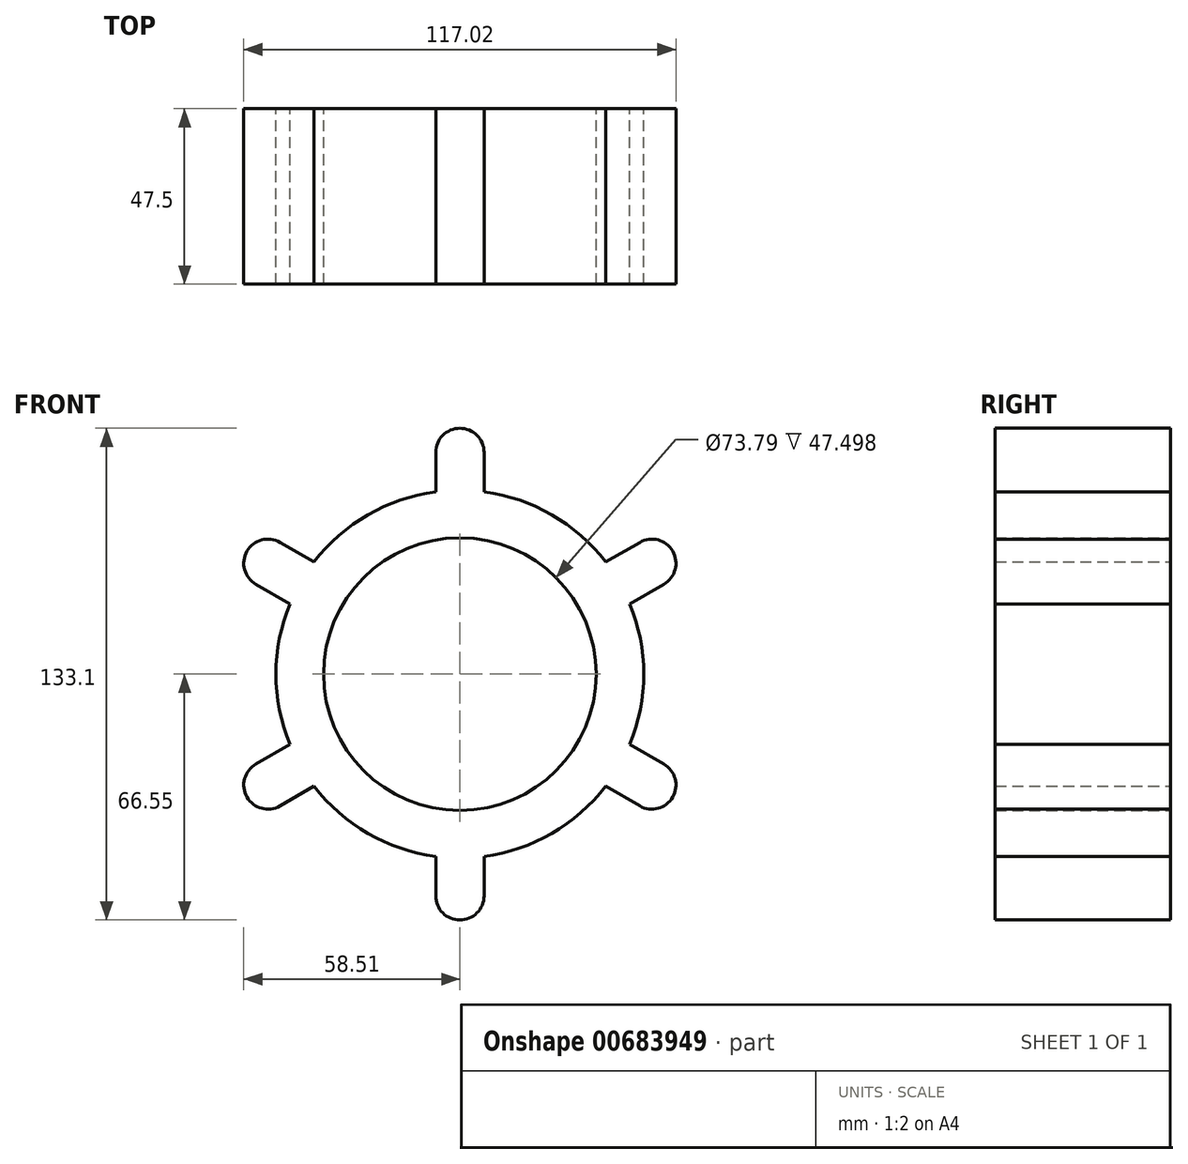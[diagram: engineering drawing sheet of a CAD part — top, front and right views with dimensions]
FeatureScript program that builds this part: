
annotation { "Feature Type Name" : "Feature", "Feature Type Description" : "" }
export const myFeature = defineFeature(function(context is Context, id is Id, definition is map)
    precondition{}
    {
        {
            var Q0;
            Q0=qCreatedBy(makeId("Front.planeOp"),FACE);
            var sketch = newSketch(context, id + "F0", { "sketchPlane" : qUnion([Q0])});
            skCircle(sketch, "E0", {"center": v(0, 0) * mm, "radius": 36.9 * mm});
            skCircle(sketch, "E1", {"center": v(0, 0) * mm, "radius": 49.79 * mm});
            skLineSegment(sketch, "E2.top", {"start": v(6.54, 39.57) * mm, "end": v(-6.54, 39.57) * mm});
            skLineSegment(sketch, "E2.left", {"start": v(6.54, 60) * mm, "end": v(6.54, 39.57) * mm});
            skLineSegment(sketch, "E2.right", {"start": v(-6.54, 60) * mm, "end": v(-6.54, 39.57) * mm});
            skPoint(sketch, "E2.middle", {"position": v(0, 49.79) * mm});
            skArc(sketch, "E3", {"start": v(6.54, 60) * mm, "mid": v(0, 66.55) * mm, "end": v(-6.54, 60) * mm});
            skLineSegment(sketch, "E4.1.0", {"start": v(-55.24, 24.34) * mm, "end": v(-37.54, 14.12) * mm});
            skArc(sketch, "E4.1.1", {"start": v(-48.7, 35.67) * mm, "mid": v(-57.63, 33.27) * mm, "end": v(-55.24, 24.34) * mm});
            skLineSegment(sketch, "E4.1.2", {"start": v(-48.7, 35.67) * mm, "end": v(-31, 25.45) * mm});
            skLineSegment(sketch, "E4.1.3", {"start": v(-31, 25.45) * mm, "end": v(-37.54, 14.12) * mm});
            skLineSegment(sketch, "E4.2.0", {"start": v(-48.7, -35.67) * mm, "end": v(-31, -25.45) * mm});
            skArc(sketch, "E4.2.1", {"start": v(-55.24, -24.34) * mm, "mid": v(-57.63, -33.27) * mm, "end": v(-48.7, -35.67) * mm});
            skLineSegment(sketch, "E4.2.2", {"start": v(-55.24, -24.34) * mm, "end": v(-37.54, -14.12) * mm});
            skLineSegment(sketch, "E4.2.3", {"start": v(-37.54, -14.12) * mm, "end": v(-31, -25.45) * mm});
            skLineSegment(sketch, "E4.3.0", {"start": v(6.54, -60) * mm, "end": v(6.54, -39.57) * mm});
            skArc(sketch, "E4.3.1", {"start": v(-6.54, -60) * mm, "mid": v(0, -66.55) * mm, "end": v(6.54, -60) * mm});
            skLineSegment(sketch, "E4.3.2", {"start": v(-6.54, -60) * mm, "end": v(-6.54, -39.57) * mm});
            skLineSegment(sketch, "E4.3.3", {"start": v(-6.54, -39.57) * mm, "end": v(6.54, -39.57) * mm});
            skLineSegment(sketch, "E4.4.0", {"start": v(55.24, -24.34) * mm, "end": v(37.54, -14.12) * mm});
            skArc(sketch, "E4.4.1", {"start": v(48.7, -35.67) * mm, "mid": v(57.63, -33.27) * mm, "end": v(55.24, -24.34) * mm});
            skLineSegment(sketch, "E4.4.2", {"start": v(48.7, -35.67) * mm, "end": v(31, -25.45) * mm});
            skLineSegment(sketch, "E4.4.3", {"start": v(31, -25.45) * mm, "end": v(37.54, -14.12) * mm});
            skLineSegment(sketch, "E4.5.0", {"start": v(48.7, 35.67) * mm, "end": v(31, 25.45) * mm});
            skArc(sketch, "E4.5.1", {"start": v(55.24, 24.34) * mm, "mid": v(57.63, 33.27) * mm, "end": v(48.7, 35.67) * mm});
            skLineSegment(sketch, "E4.5.2", {"start": v(55.24, 24.34) * mm, "end": v(37.54, 14.12) * mm});
            skLineSegment(sketch, "E4.5.3", {"start": v(37.54, 14.12) * mm, "end": v(31, 25.45) * mm});
            skSolve(sketch);
        }
        {
            var Q0;
            Q0=makeQuery(id+"F0.imprint","IMPRINT",FACE,{"disambiguationData":[TD([[makeQuery(id+"F0.imprint","IMPRINT",EDGE,{"derivedFrom":sQuery(id+"F0.wireOp",EDGE,"E0")}),-1.0]])]});
            var Q1;
            {var subQ5=sQuery(id+"F0.wireOp",EDGE,"E4.1.3");Q1=makeQuery(id+"F0.imprint","IMPRINT",FACE,{"disambiguationData":[TD([[makeQuery(id+"F0.imprint","IMPRINT",EDGE,{"derivedFrom":subQ5}),-1.0]])]});}
            var Q2;
            {var subQ5=sQuery(id+"F0.wireOp",EDGE,"E4.1.1");Q2=makeQuery(id+"F0.imprint","IMPRINT",FACE,{"disambiguationData":[TD([[makeQuery(id+"F0.imprint","IMPRINT",EDGE,{"derivedFrom":subQ5}),1.0]])]});}
            var Q3;
            {var subQ5=sQuery(id+"F0.wireOp",EDGE,"E4.2.3");Q3=makeQuery(id+"F0.imprint","IMPRINT",FACE,{"disambiguationData":[TD([[makeQuery(id+"F0.imprint","IMPRINT",EDGE,{"derivedFrom":subQ5}),-1.0]])]});}
            var Q4;
            {var subQ5=sQuery(id+"F0.wireOp",EDGE,"E4.2.1");Q4=makeQuery(id+"F0.imprint","IMPRINT",FACE,{"disambiguationData":[TD([[makeQuery(id+"F0.imprint","IMPRINT",EDGE,{"derivedFrom":subQ5}),1.0]])]});}
            var Q5;
            {var subQ5=sQuery(id+"F0.wireOp",EDGE,"E4.3.1");Q5=makeQuery(id+"F0.imprint","IMPRINT",FACE,{"disambiguationData":[TD([[makeQuery(id+"F0.imprint","IMPRINT",EDGE,{"derivedFrom":subQ5}),1.0]])]});}
            var Q6;
            {var subQ5=sQuery(id+"F0.wireOp",EDGE,"E4.3.3");Q6=makeQuery(id+"F0.imprint","IMPRINT",FACE,{"disambiguationData":[TD([[makeQuery(id+"F0.imprint","IMPRINT",EDGE,{"derivedFrom":subQ5}),-1.0]])]});}
            var Q7;
            {var subQ5=sQuery(id+"F0.wireOp",EDGE,"E4.4.3");Q7=makeQuery(id+"F0.imprint","IMPRINT",FACE,{"disambiguationData":[TD([[makeQuery(id+"F0.imprint","IMPRINT",EDGE,{"derivedFrom":subQ5}),-1.0]])]});}
            var Q8;
            {var subQ5=sQuery(id+"F0.wireOp",EDGE,"E4.4.1");Q8=makeQuery(id+"F0.imprint","IMPRINT",FACE,{"disambiguationData":[TD([[makeQuery(id+"F0.imprint","IMPRINT",EDGE,{"derivedFrom":subQ5}),1.0]])]});}
            var Q9;
            {var subQ5=sQuery(id+"F0.wireOp",EDGE,"E4.5.3");Q9=makeQuery(id+"F0.imprint","IMPRINT",FACE,{"disambiguationData":[TD([[makeQuery(id+"F0.imprint","IMPRINT",EDGE,{"derivedFrom":subQ5}),-1.0]])]});}
            var Q10;
            {var subQ5=sQuery(id+"F0.wireOp",EDGE,"E4.5.1");Q10=makeQuery(id+"F0.imprint","IMPRINT",FACE,{"disambiguationData":[TD([[makeQuery(id+"F0.imprint","IMPRINT",EDGE,{"derivedFrom":subQ5}),1.0]])]});}
            var Q11;
            {var subQ5=sQuery(id+"F0.wireOp",EDGE,"E2.top");Q11=makeQuery(id+"F0.imprint","IMPRINT",FACE,{"disambiguationData":[TD([[makeQuery(id+"F0.imprint","IMPRINT",EDGE,{"derivedFrom":subQ5}),-1.0]])]});}
            var Q12;
            {var subQ5=sQuery(id+"F0.wireOp",EDGE,"E3");Q12=makeQuery(id+"F0.imprint","IMPRINT",FACE,{"disambiguationData":[TD([[makeQuery(id+"F0.imprint","IMPRINT",EDGE,{"derivedFrom":subQ5}),1.0]])]});}
            extrude(context, id + "F1", {"entities" : qUnion([Q0, Q1, Q2, Q3, Q4, Q5, Q6, Q7, Q8, Q9, Q10, Q11, Q12]), "depth" : 5.08 * mm, "offsetDistance" : 25.4 * mm});
        }
        {
            var Q0;
            Q0=makeQuery(id+"F1.opExtrude","CAP_FACE",FACE,{"disambiguationData":[OSD([sQuery(id+"F0.wireOp",EDGE,"E0"),sQuery(id+"F0.wireOp",EDGE,"E1"),sQuery(id+"F0.wireOp",EDGE,"E2.left"),sQuery(id+"F0.wireOp",EDGE,"E2.right"),sQuery(id+"F0.wireOp",EDGE,"E3"),sQuery(id+"F0.wireOp",EDGE,"E4.1.0"),sQuery(id+"F0.wireOp",EDGE,"E4.1.1"),sQuery(id+"F0.wireOp",EDGE,"E4.1.2"),sQuery(id+"F0.wireOp",EDGE,"E4.2.0"),sQuery(id+"F0.wireOp",EDGE,"E4.2.1"),sQuery(id+"F0.wireOp",EDGE,"E4.2.2"),sQuery(id+"F0.wireOp",EDGE,"E4.3.0"),sQuery(id+"F0.wireOp",EDGE,"E4.3.1"),sQuery(id+"F0.wireOp",EDGE,"E4.3.2"),sQuery(id+"F0.wireOp",EDGE,"E4.4.0"),sQuery(id+"F0.wireOp",EDGE,"E4.4.1"),sQuery(id+"F0.wireOp",EDGE,"E4.4.2"),sQuery(id+"F0.wireOp",EDGE,"E4.5.0"),sQuery(id+"F0.wireOp",EDGE,"E4.5.1"),sQuery(id+"F0.wireOp",EDGE,"E4.5.2")])],"isStart":false});
            extrude(context, id + "F2", {"entities" : qUnion([Q0]), "operationType" : NewBodyOperationType.ADD, "depth" : 42.42 * mm, "offsetDistance" : 25.4 * mm});
        }
    });
